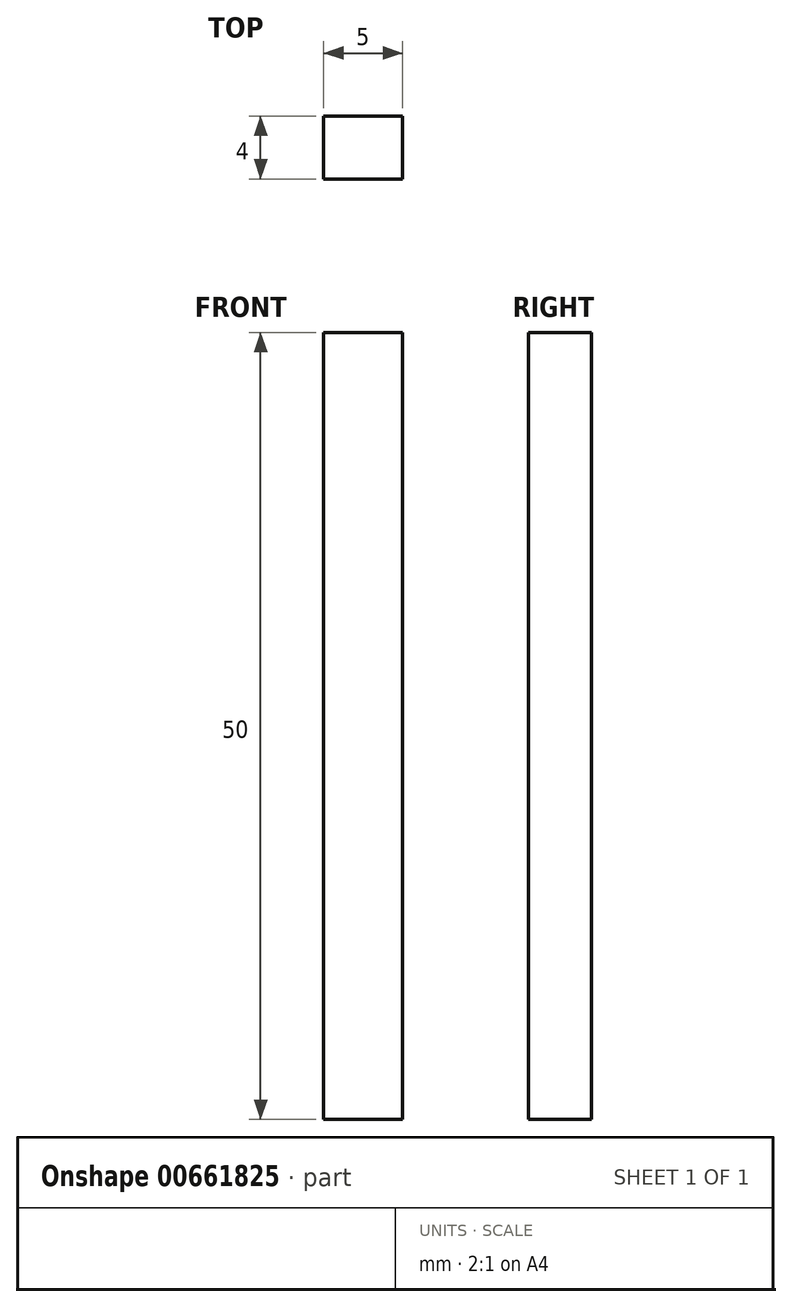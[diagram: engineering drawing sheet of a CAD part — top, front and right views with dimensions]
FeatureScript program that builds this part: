
annotation { "Feature Type Name" : "Feature", "Feature Type Description" : "" }
export const myFeature = defineFeature(function(context is Context, id is Id, definition is map)
    precondition{}
    {
        {
            var Q0;
            Q0=qCreatedBy(makeId("Top.planeOp"),FACE);
            var sketch = newSketch(context, id + "F0", { "sketchPlane" : qUnion([Q0])});
            skLineSegment(sketch, "E0.bottom", {"start": v(2.5, -2) * mm, "end": v(-2.5, -2) * mm});
            skLineSegment(sketch, "E0.top", {"start": v(2.5, 2) * mm, "end": v(-2.5, 2) * mm});
            skLineSegment(sketch, "E0.left", {"start": v(2.5, -2) * mm, "end": v(2.5, 2) * mm});
            skLineSegment(sketch, "E0.right", {"start": v(-2.5, -2) * mm, "end": v(-2.5, 2) * mm});
            skPoint(sketch, "E0.middle", {"position": v(0, 0) * mm});
            skSolve(sketch);
        }
        {
            var Q0;
            Q0 = qSketchRegion(id + "F0", true);
            extrude(context, id + "F1", {"entities" : qUnion([Q0]), "depth" : 50 * mm, "offsetDistance" : 25.4 * mm});
        }
    });
